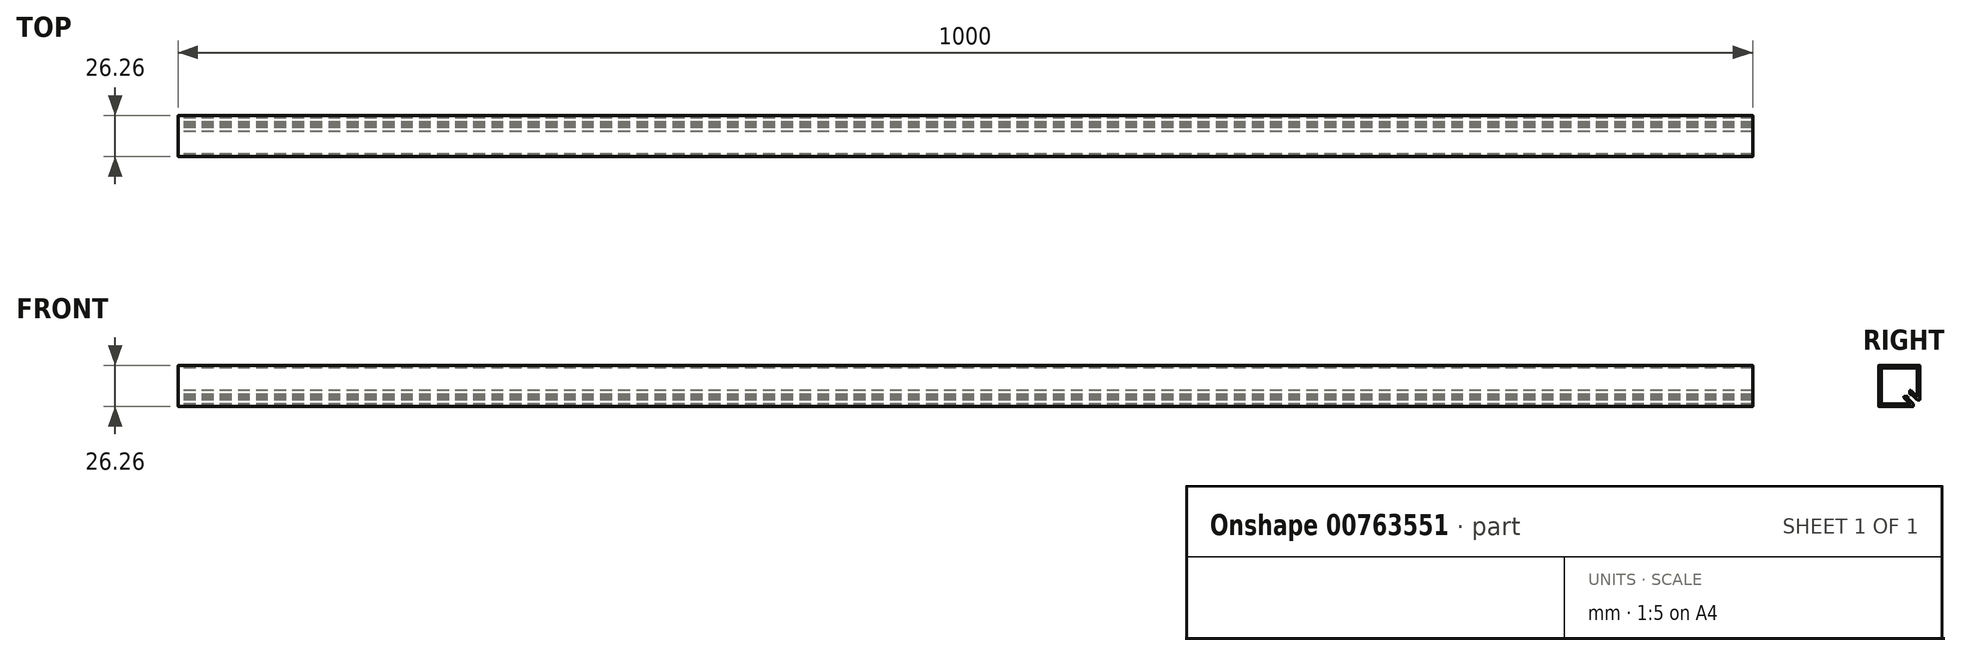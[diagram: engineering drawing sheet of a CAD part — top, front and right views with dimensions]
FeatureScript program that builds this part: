
annotation { "Feature Type Name" : "Feature", "Feature Type Description" : "" }
export const myFeature = defineFeature(function(context is Context, id is Id, definition is map)
    precondition{}
    {
        {
            var Q0;
            Q0=qCreatedBy(makeId("Right.planeOp"),FACE);
            var sketch = newSketch(context, id + "F0", { "sketchPlane" : qUnion([Q0])});
            skLineSegment(sketch, "E0.bottom", {"start": v(25.96, 26.26) * mm, "end": v(0.3, 26.26) * mm});
            skLineSegment(sketch, "E0.top", {"start": v(21.7, 0) * mm, "end": v(0.3, 0) * mm});
            skPoint(sketch, "E0.middle", {"position": v(0, 0) * mm});
            skLineSegment(sketch, "E1", {"start": v(22, 0.3) * mm, "end": v(22, 1.48) * mm});
            skLineSegment(sketch, "E2", {"start": v(1.9, 24.66) * mm, "end": v(24.36, 24.66) * mm});
            skLineSegment(sketch, "E3", {"start": v(26.26, 4.56) * mm, "end": v(26.26, 25.96) * mm});
            skPoint(sketch, "E4.orphan", {"position": v(15.9, 0) * mm});
            skLineSegment(sketch, "E5", {"start": v(22, -2.28) * mm, "end": v(22, 1.6) * mm});
            skPoint(sketch, "E6.start.orphan", {"position": v(6.74, 0) * mm});
            skLineSegment(sketch, "E7.trimOffspring", {"start": v(19.58, 1.6) * mm, "end": v(1.9, 1.6) * mm});
            skLineSegment(sketch, "E8.trimOffspring", {"start": v(24.66, 6.69) * mm, "end": v(24.66, 24.36) * mm});
            skPoint(sketch, "E9.visualSharp", {"position": v(23.6, 0) * mm});
            skPoint(sketch, "E10.visualSharp", {"position": v(30.96, 4.68) * mm});
            skPoint(sketch, "E11.visualSharp", {"position": v(9.15, 7.2) * mm});
            skLineSegment(sketch, "E12", {"start": v(0, 0.3) * mm, "end": v(0, 25.96) * mm});
            skLineSegment(sketch, "E13", {"start": v(1.6, 24.36) * mm, "end": v(1.6, 1.9) * mm});
            skPoint(sketch, "E14.end.orphan", {"position": v(7.64, 6.95) * mm});
            skPoint(sketch, "E15.visualSharp", {"position": v(22, -1.17) * mm});
            skPoint(sketch, "E16.visualSharp", {"position": v(7.03, 1.85) * mm});
            skPoint(sketch, "E17.end.orphan", {"position": v(4.37, 1.6) * mm});
            skPoint(sketch, "E18.start.orphan", {"position": v(33.48, 11.89) * mm});
            skPoint(sketch, "E10.filletArc.end.orphan", {"position": v(30.82, 10.54) * mm});
            skLineSegment(sketch, "E19", {"start": v(16.03, 5.87) * mm, "end": v(19.8, 2.11) * mm});
            skPoint(sketch, "E20.end.orphan", {"position": v(15.52, 2.5) * mm});
            skLineSegment(sketch, "E21", {"start": v(21.91, 1.69) * mm, "end": v(18.46, 5.14) * mm});
            skLineSegment(sketch, "E22", {"start": v(18.21, 6.39) * mm, "end": v(16.24, 6.39) * mm});
            skLineSegment(sketch, "E23", {"start": v(18.46, 5.14) * mm, "end": v(18.46, 6.14) * mm});
            skLineSegment(sketch, "E24", {"start": v(24.15, 6.47) * mm, "end": v(20.4, 10.23) * mm});
            skLineSegment(sketch, "E25", {"start": v(21.13, 7.8) * mm, "end": v(20.13, 7.8) * mm});
            skLineSegment(sketch, "E26", {"start": v(19.88, 8.05) * mm, "end": v(19.88, 10.02) * mm});
            skLineSegment(sketch, "E27", {"start": v(25.96, 4.26) * mm, "end": v(24.79, 4.26) * mm});
            skLineSegment(sketch, "E28", {"start": v(24.58, 4.35) * mm, "end": v(21.13, 7.8) * mm});
            skPoint(sketch, "E29.visualSharp", {"position": v(19.88, 7.8) * mm});
            skArc(sketch, "E29.filletArc", {"start": v(19.88, 8.05) * mm, "mid": v(19.95, 7.87) * mm, "end": v(20.13, 7.8) * mm});
            skPoint(sketch, "E30.visualSharp", {"position": v(18.46, 6.39) * mm});
            skArc(sketch, "E30.filletArc", {"start": v(18.46, 6.14) * mm, "mid": v(18.4, 6.31) * mm, "end": v(18.21, 6.39) * mm});
            skPoint(sketch, "E31.visualSharp", {"position": v(19.88, 10.75) * mm});
            skArc(sketch, "E31.filletArc", {"start": v(20.4, 10.23) * mm, "mid": v(20.06, 10.3) * mm, "end": v(19.88, 10.02) * mm});
            skPoint(sketch, "E32.visualSharp", {"position": v(15.52, 6.39) * mm});
            skArc(sketch, "E32.filletArc", {"start": v(16.24, 6.39) * mm, "mid": v(15.96, 6.2) * mm, "end": v(16.03, 5.87) * mm});
            skPoint(sketch, "E33.visualSharp", {"position": v(20.3, 1.6) * mm});
            skArc(sketch, "E33.filletArc", {"start": v(19.58, 1.6) * mm, "mid": v(19.86, 1.79) * mm, "end": v(19.8, 2.11) * mm});
            skPoint(sketch, "E34.visualSharp", {"position": v(24.66, 5.96) * mm});
            skArc(sketch, "E34.filletArc", {"start": v(24.15, 6.47) * mm, "mid": v(24.48, 6.4) * mm, "end": v(24.66, 6.69) * mm});
            skPoint(sketch, "E35.visualSharp", {"position": v(24.66, 4.26) * mm});
            skArc(sketch, "E35.filletArc", {"start": v(24.58, 4.35) * mm, "mid": v(24.67, 4.29) * mm, "end": v(24.79, 4.26) * mm});
            skPoint(sketch, "E36.visualSharp", {"position": v(22, 1.6) * mm});
            skArc(sketch, "E36.filletArc", {"start": v(22, 1.48) * mm, "mid": v(21.98, 1.6) * mm, "end": v(21.91, 1.69) * mm});
            skPoint(sketch, "E37.visualSharp", {"position": v(26.26, 4.26) * mm});
            skArc(sketch, "E37.filletArc", {"start": v(25.96, 4.26) * mm, "mid": v(26.18, 4.35) * mm, "end": v(26.26, 4.56) * mm});
            skPoint(sketch, "E38.visualSharp", {"position": v(22, 0) * mm});
            skArc(sketch, "E38.filletArc", {"start": v(21.7, 0) * mm, "mid": v(21.91, 0.09) * mm, "end": v(22, 0.3) * mm});
            skArc(sketch, "E39.filletArc", {"start": v(0, 0.3) * mm, "mid": v(0.09, 0.09) * mm, "end": v(0.3, 0) * mm});
            skPoint(sketch, "E40.visualSharp", {"position": v(1.6, 1.6) * mm});
            skArc(sketch, "E40.filletArc", {"start": v(1.6, 1.9) * mm, "mid": v(1.69, 1.69) * mm, "end": v(1.9, 1.6) * mm});
            skPoint(sketch, "E41.visualSharp", {"position": v(1.6, 24.66) * mm});
            skArc(sketch, "E41.filletArc", {"start": v(1.9, 24.66) * mm, "mid": v(1.69, 24.58) * mm, "end": v(1.6, 24.36) * mm});
            skPoint(sketch, "E42.visualSharp", {"position": v(0, 26.26) * mm});
            skArc(sketch, "E42.filletArc", {"start": v(0.3, 26.26) * mm, "mid": v(0.09, 26.18) * mm, "end": v(0, 25.96) * mm});
            skPoint(sketch, "E43.visualSharp", {"position": v(24.66, 24.66) * mm});
            skArc(sketch, "E43.filletArc", {"start": v(24.66, 24.36) * mm, "mid": v(24.58, 24.58) * mm, "end": v(24.36, 24.66) * mm});
            skPoint(sketch, "E44.visualSharp", {"position": v(26.26, 26.26) * mm});
            skArc(sketch, "E44.filletArc", {"start": v(26.26, 25.96) * mm, "mid": v(26.18, 26.18) * mm, "end": v(25.96, 26.26) * mm});
            skLineSegment(sketch, "E45", {"start": v(26.26, 4.56) * mm, "end": v(26.26, 0) * mm, "construction": true});
            skLineSegment(sketch, "E46", {"start": v(21.7, 0) * mm, "end": v(21.7, 0) * mm});
            skLineSegment(sketch, "E47", {"start": v(21.7, 0) * mm, "end": v(26.26, 0) * mm, "construction": true});
            skLineSegment(sketch, "E48", {"start": v(26.26, 0) * mm, "end": v(21.91, 1.69) * mm, "construction": true});
            skLineSegment(sketch, "E49", {"start": v(24.58, 4.35) * mm, "end": v(26.26, 0) * mm, "construction": true});
            skSolve(sketch);
        }
        {
            var Q0;
            Q0=qSketchRegion(id+"F0",true);
            extrude(context, id + "F1", {"entities" : qUnion([Q0]), "depth" : 1000 * mm, "offsetDistance" : 25 * mm});
        }
    });
